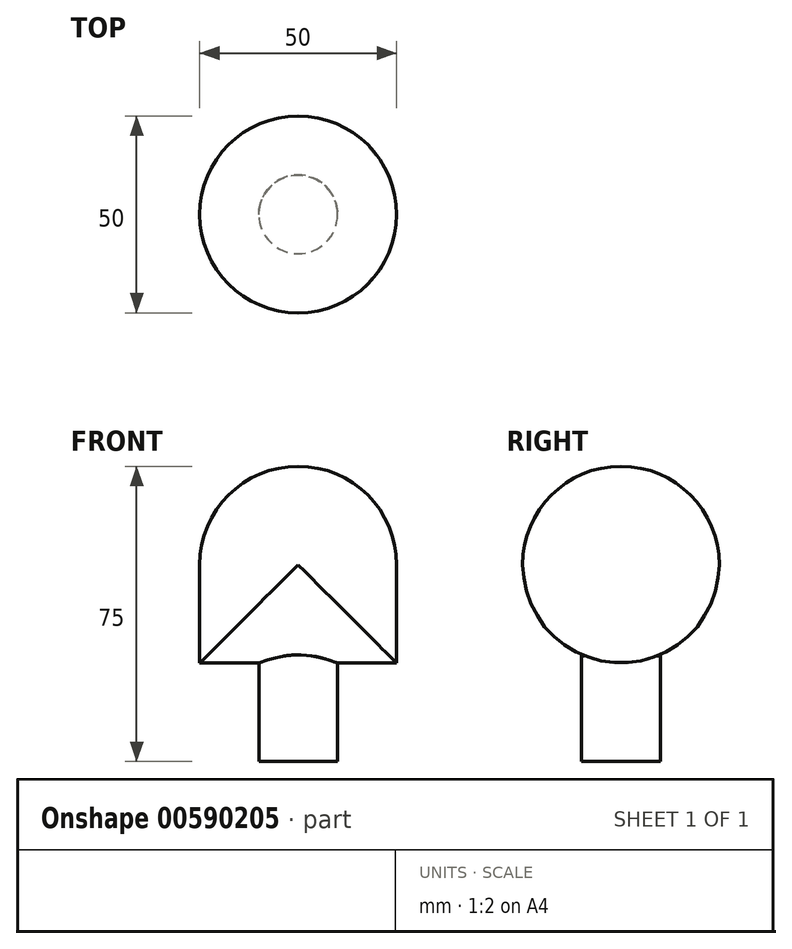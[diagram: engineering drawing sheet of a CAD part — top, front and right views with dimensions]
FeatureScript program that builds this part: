
annotation { "Feature Type Name" : "Feature", "Feature Type Description" : "" }
export const myFeature = defineFeature(function(context is Context, id is Id, definition is map)
    precondition{}
    {
        {
            var Q0;
            Q0=qCreatedBy(makeId("Top.planeOp"),FACE);
            var sketch = newSketch(context, id + "F0", { "sketchPlane" : qUnion([Q0])});
            skCircle(sketch, "E0", {"center": v(0, 0) * mm, "radius": 10 * mm});
            skSolve(sketch);
        }
        {
            var Q0;
            Q0 = qSketchRegion(id + "F0", true);
            extrude(context, id + "F1", {"entities" : qUnion([Q0]), "depth" : 25 * mm, "offsetDistance" : 25 * mm});
        }
        {
            var Q0;
            Q0=makeQuery(id+"F1.opExtrude","CAP_FACE",FACE,{"disambiguationData":[OSD([sQuery(id+"F0.wireOp",EDGE,"E0")])],"isStart":false});
            var sketch = newSketch(context, id + "F2", { "sketchPlane" : qUnion([Q0])});
            skLineSegment(sketch, "E1.bottom", {"start": v(25, 25) * mm, "end": v(-25, 25) * mm});
            skLineSegment(sketch, "E1.top", {"start": v(25, -25) * mm, "end": v(-25, -25) * mm});
            skLineSegment(sketch, "E1.left", {"start": v(25, 25) * mm, "end": v(25, -25) * mm});
            skLineSegment(sketch, "E1.right", {"start": v(-25, 25) * mm, "end": v(-25, -25) * mm});
            skPoint(sketch, "E1.middle", {"position": v(0, 0) * mm});
            skSolve(sketch);
        }
        {
            var Q0;
            Q0 = qSketchRegion(id + "F2", true);
            extrude(context, id + "F3", {"entities" : qUnion([Q0]), "operationType" : NewBodyOperationType.ADD, "depth" : 50 * mm, "offsetDistance" : 25 * mm});
        }
        {
            var Q0;
            Q0=makeQuery(id+"F3.opExtrude","SWEPT_FACE",FACE,{"disambiguationData":[OSD([sQuery(id+"F2.wireOp",EDGE,"E1.top")])]});
            var Q1;
            Q1=makeQuery(id+"F3.opExtrude","SWEPT_FACE",FACE,{"disambiguationData":[OSD([sQuery(id+"F2.wireOp",EDGE,"E1.bottom")])]});
            var Q2;
            Q2=makeQuery(id+"F3.opExtrude","CAP_FACE",FACE,{"disambiguationData":[OSD([sQuery(id+"F2.wireOp",EDGE,"E1.bottom"),sQuery(id+"F2.wireOp",EDGE,"E1.top"),sQuery(id+"F2.wireOp",EDGE,"E1.left"),sQuery(id+"F2.wireOp",EDGE,"E1.right")])],"isStart":false});
            fillet(context, id + "F4", {"entities" : qUnion([Q0, Q1, Q2]), "radius" : 25 * mm, "tangentPropagation" : true, "allowEdgeOverflow" : false});
        }
    });
